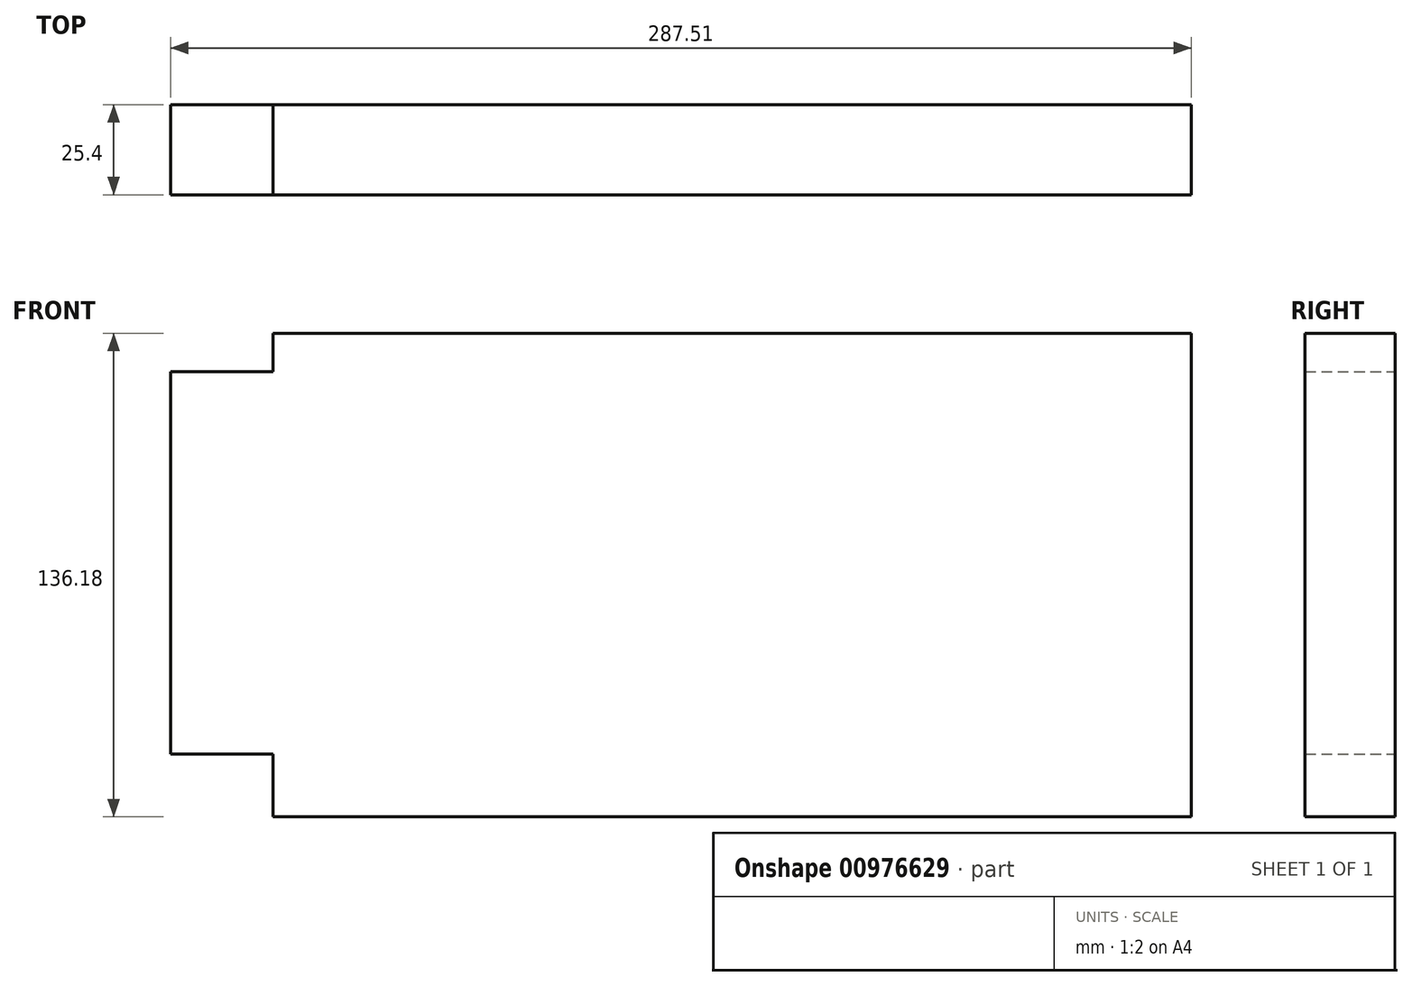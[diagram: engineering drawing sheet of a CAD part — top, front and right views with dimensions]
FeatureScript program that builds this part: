
annotation { "Feature Type Name" : "Feature", "Feature Type Description" : "" }
export const myFeature = defineFeature(function(context is Context, id is Id, definition is map)
    precondition{}
    {
        {
            var Q0;
            Q0=qCreatedBy(makeId("Front.planeOp"),FACE);
            var sketch = newSketch(context, id + "F0", { "sketchPlane" : qUnion([Q0])});
            skLineSegment(sketch, "E0.bottom", {"start": v(-144.66, 58.19) * mm, "end": v(143.21, 58.19) * mm});
            skLineSegment(sketch, "E0.top", {"start": v(-144.66, -49.54) * mm, "end": v(143.21, -49.54) * mm});
            skLineSegment(sketch, "E0.left", {"start": v(-144.66, 58.19) * mm, "end": v(-144.66, -49.54) * mm});
            skLineSegment(sketch, "E0.right", {"start": v(143.21, 58.19) * mm, "end": v(143.21, -49.54) * mm});
            skLineSegment(sketch, "E1.bottom", {"start": v(-115.83, 69) * mm, "end": v(142.85, 69) * mm});
            skLineSegment(sketch, "E1.top", {"start": v(-115.83, -67.2) * mm, "end": v(142.85, -67.2) * mm});
            skLineSegment(sketch, "E1.left", {"start": v(-115.83, 69) * mm, "end": v(-115.83, -67.2) * mm});
            skLineSegment(sketch, "E1.right", {"start": v(142.85, 69) * mm, "end": v(142.85, -67.2) * mm});
            skSolve(sketch);
        }
        {
            var Q0;
            Q0=qCreatedBy(makeId("Front.planeOp"),FACE);
            var sketch = newSketch(context, id + "F1", { "sketchPlane" : qUnion([Q0])});
            skSolve(sketch);
        }
        {
            var Q0;
            Q0 = qSketchRegion(id + "F1", true);
            var Q1;
            {var subQ0=sQuery(id+"F0.wireOp",EDGE,"E0.left");Q1=makeQuery(id+"F0.imprint","IMPRINT",FACE,{"disambiguationData":[TD([[makeQuery(id+"F0.imprint","IMPRINT",EDGE,{"derivedFrom":subQ0}),1.0]])]});}
            var Q2;
            {var subQ5=sQuery(id+"F0.wireOp",EDGE,"E1.top");Q2=makeQuery(id+"F0.imprint","IMPRINT",FACE,{"disambiguationData":[TD([[makeQuery(id+"F0.imprint","IMPRINT",EDGE,{"derivedFrom":subQ5}),1.0]])]});}
            var Q3;
            {var subQ5=sQuery(id+"F0.wireOp",EDGE,"E1.bottom");Q3=makeQuery(id+"F0.imprint","IMPRINT",FACE,{"disambiguationData":[TD([[makeQuery(id+"F0.imprint","IMPRINT",EDGE,{"derivedFrom":subQ5}),-1.0]])]});}
            var Q4;
            {var subQ0=sQuery(id+"F0.wireOp",EDGE,"E1.left");var subQ1=sQuery(id+"F0.wireOp",EDGE,"E0.bottom");var subQ2=makeQuery(id+"F0.imprint","INTERSECT",VERTEX,{"derivedFrom":[subQ1,subQ0]});Q4=makeQuery(id+"F0.imprint","IMPRINT",FACE,{"disambiguationData":[TD([[makeQuery(id+"F0.imprint","IMPRINT",EDGE,{"disambiguationData":[TD([[subQ2,-1.0]])],"derivedFrom":subQ1}),-1.0]])]});}
            extrude(context, id + "F2", {"entities" : qUnion([Q0, Q1, Q2, Q3, Q4]), "depth" : 25.4 * mm, "offsetDistance" : 25.4 * mm});
        }
    });
